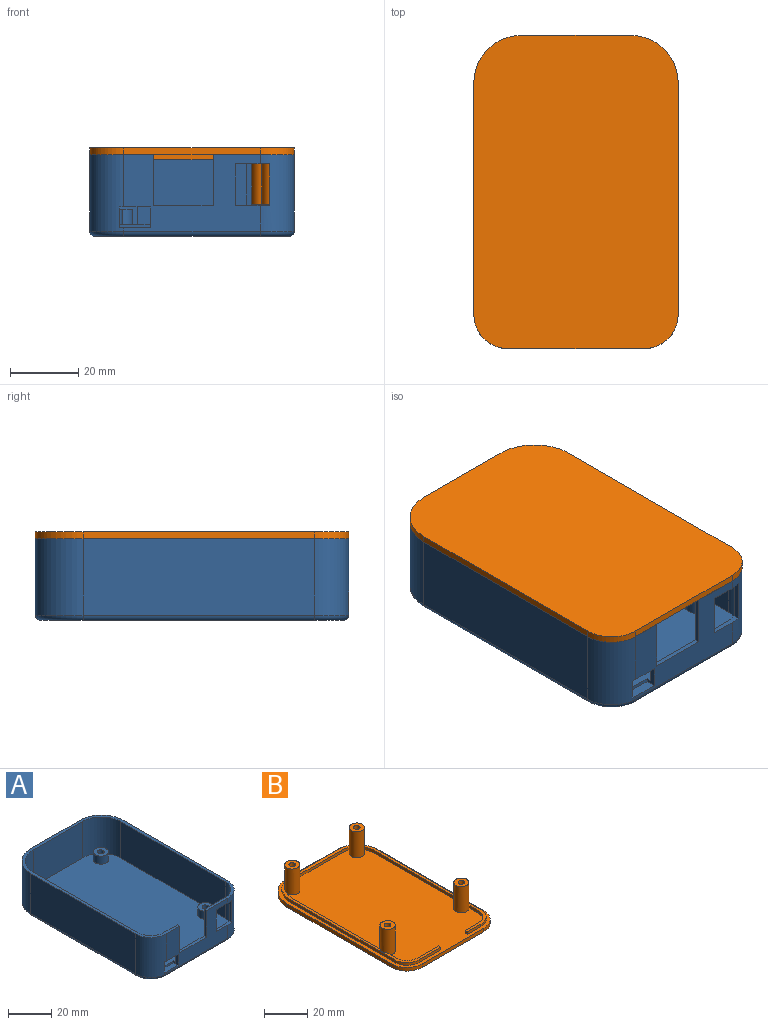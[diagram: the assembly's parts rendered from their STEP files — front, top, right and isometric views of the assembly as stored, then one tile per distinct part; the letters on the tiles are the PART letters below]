
ASSEMBLY  parts=2 mates=1
PART A: 59 faces, bbox 62.3x94x24 mm
  f0: plane 40x22.5mm, normal (0,-1,0), area 500.7mm2, adj f1,f2,f3,f39,f40,f42,f44,f45
  f1: plane 92x60mm, normal (0,0,1), area 391.8mm2, adj f0,f2,f3,f4,f5,f6,f11,f12
  f2: cylinder r=10mm len=22.5mm, axis (0,0,1), area 317.2mm2, adj f0,f1,f11,f45,f46,f47,f55
  f3: cylinder r=10mm len=22.5mm, axis (0,0,-1), area 345.5mm2, adj f0,f1,f13,f40,f41,f42,f51
  f4: plane 40x20.5mm, normal (0,1,0), area 428.4mm2, adj f1,f5,f6,f20,f39,f40,f44,f45
  f5: cylinder r=8.5mm len=20.5mm, axis (0,0,1), area 237.3mm2, adj f1,f4,f17,f20,f45,f46,f47
  f6: cylinder r=8.5mm len=20.5mm, axis (0,0,-1), area 267.1mm2, adj f1,f4,f19,f20,f40,f41
  f7: cylinder r=1.5mm len=6mm, axis (0,0,1), area 56.5mm2, adj f24,f37
  f8: cylinder r=1.5mm len=6mm, axis (0,0,1), area 56.5mm2, adj f30,f35
  f9: cylinder r=1.5mm len=6mm, axis (0,0,1), area 56.5mm2, adj f26,f33
  f10: cylinder r=1.5mm len=6mm, axis (0,0,1), area 56.5mm2, adj f28,f31
  f11: plane 68x22.5mm, normal (1,0,0), area 1530mm2, adj f1,f2,f15,f57
  f12: plane 32x22.5mm, normal (0,1,0), area 720mm2, adj f1,f15,f16,f56
  f13: plane 68x22.5mm, normal (-1,0,0), area 1530mm2, adj f1,f3,f16,f52
  f14: plane 89x57mm, normal (0,0,-1), area 4896.4mm2, adj f32,f34,f36,f38,f51,f52,f53,f54
  f15: cylinder r=14mm len=22.5mm, axis (0,0,-1), area 494.8mm2, adj f1,f11,f12,f58
  f16: cylinder r=14mm len=22.5mm, axis (0,0,1), area 494.8mm2, adj f1,f12,f13,f54
  f17: plane 68x20.5mm, normal (-1,0,0), area 1394mm2, adj f1,f5,f20,f21
  f18: plane 32x20.5mm, normal (0,-1,0), area 656mm2, adj f1,f20,f21,f22
  f19: plane 68x20.5mm, normal (1,0,0), area 1394mm2, adj f1,f6,f20,f22
  f20: plane 89x57mm, normal (0,0,1), area 4807.5mm2, adj f4,f5,f6,f17,f18,f19,f21,f22
  f21: cylinder r=12.5mm len=20.5mm, axis (0,0,-1), area 402.5mm2, adj f1,f17,f18,f20
  f22: cylinder r=12.5mm len=20.5mm, axis (0,0,1), area 402.5mm2, adj f1,f18,f19,f20
  f23: cylinder r=3.5mm len=7mm, axis (0,0,-1), area 99mm2, adj f20,f24
  f24: plane 7x7mm, normal (0,0,1), area 31.4mm2, adj f7,f23
  f25: cylinder r=3.5mm len=7mm, axis (0,0,-1), area 99mm2, adj f20,f26
  f26: plane 7x7mm, normal (0,0,1), area 31.4mm2, adj f9,f25
  f27: cylinder r=3.5mm len=7mm, axis (0,0,-1), area 99mm2, adj f20,f28
  f28: plane 7x7mm, normal (0,0,1), area 31.4mm2, adj f10,f27
  f29: cylinder r=3.5mm len=7mm, axis (0,0,-1), area 99mm2, adj f20,f30
  f30: plane 7x7mm, normal (0,0,1), area 31.4mm2, adj f8,f29
  f31: plane 5x5mm, normal (0,0,-1), area 12.6mm2, adj f10,f32
  f32: cylinder r=2.5mm len=5mm, axis (0,0,-1), area 31.4mm2, adj f14,f31
  f33: plane 5x5mm, normal (0,0,-1), area 12.6mm2, adj f9,f34
  f34: cylinder r=2.5mm len=5mm, axis (0,0,-1), area 31.4mm2, adj f14,f33
  f35: plane 5x5mm, normal (0,0,-1), area 12.6mm2, adj f8,f36
  f36: cylinder r=2.5mm len=5mm, axis (0,0,-1), area 31.4mm2, adj f14,f35
  f37: plane 5x5mm, normal (0,0,-1), area 12.6mm2, adj f7,f38
  f38: cylinder r=2.5mm len=5mm, axis (0,0,-1), area 31.4mm2, adj f14,f37
  f39: plane 6.1x3mm, normal (-1,0,0), area 10.7mm2, adj f0,f4,f20,f40,f42,f43
  f40: plane 9x1.6mm, normal (0,0,-1), area 13.5mm2, adj f0,f3,f4,f6,f39,f41
  f41: plane 6.1x2.92mm, normal (1,0,0), area 10.6mm2, adj f3,f6,f20,f40,f42,f43
  f42: plane 9x3mm, normal (0,0,1), area 27mm2, adj f0,f3,f39,f41,f43
  f43: plane 9x1mm, normal (0,-1,0), area 9mm2, adj f20,f39,f41,f42
  f44: plane 12.3x1.5mm, normal (1,0,0), area 18.5mm2, adj f0,f4,f45,f46
  f45: plane 10.2x2.01mm, normal (0,0,-1), area 15.4mm2, adj f0,f2,f4,f5,f44,f47
  f46: plane 10.2x2.01mm, normal (0,0,1), area 15.4mm2, adj f0,f2,f4,f5,f44,f47
  f47: plane 12.3x1.58mm, normal (-1,0,0), area 19.4mm2, adj f2,f5,f45,f46
  f48: plane 15x1.5mm, normal (1,0,0), area 22.5mm2, adj f0,f1,f4,f49
  f49: plane 17.5x1.5mm, normal (0,0,1), area 26.3mm2, adj f0,f4,f48,f50
  f50: plane 15x1.5mm, normal (-1,0,0), area 22.5mm2, adj f0,f1,f4,f49
  f51: torus R=8.5mm, axis (0,0,1), area 35mm2, adj f3,f14,f52,f53
  f52: cylinder r=1.5mm len=68mm, axis (0,-1,0), area 160.2mm2, adj f13,f14,f51,f54
  f53: cylinder r=1.5mm len=40mm, axis (1,0,0), area 94.2mm2, adj f0,f14,f51,f55
  f54: torus R=12.5mm, axis (0,0,1), area 49.8mm2, adj f14,f16,f52,f56
  f55: torus R=8.5mm, axis (0,0,1), area 35mm2, adj f2,f14,f53,f57
  f56: cylinder r=1.5mm len=32mm, axis (-1,0,0), area 75.4mm2, adj f12,f14,f54,f58
  f57: cylinder r=1.5mm len=68mm, axis (0,1,0), area 160.2mm2, adj f11,f14,f55,f58
  f58: torus R=12.5mm, axis (0,0,1), area 49.8mm2, adj f14,f15,f56,f57
PART B: 51 faces, bbox 60x92x16.6 mm
  f0: plane 92x60mm, normal (0,0,1), area 4870mm2, adj f1,f2,f3,f4,f5,f6,f7,f8
  f1: plane 57.27x1.5mm, normal (-1,0,0), area 85.9mm2, adj f0,f2,f34,f47
  f2: cylinder r=10.7mm len=6.83mm, axis (0,0,-1), area 11.1mm2, adj f0,f1,f34,f43
  f3: plane 6.27x1.5mm, normal (1,0,0), area 9.4mm2, adj f0,f16,f34,f40
  f4: plane 57.27x1.5mm, normal (1,0,0), area 85.9mm2, adj f0,f6,f34,f40
  f5: cylinder r=10.7mm len=6.01mm, axis (0,0,-1), area 9.6mm2, adj f0,f17,f34,f36
  f6: cylinder r=10.7mm len=6.83mm, axis (0,0,-1), area 11.1mm2, adj f0,f4,f34,f36
  f7: plane 40x2mm, normal (0,-1,0), area 80mm2, adj f0,f11,f12,f13
  f8: plane 68x2mm, normal (1,0,0), area 136mm2, adj f0,f11,f12,f14
  f9: plane 32x2mm, normal (0,1,0), area 64mm2, adj f0,f11,f14,f15
  f10: plane 68x2mm, normal (-1,0,0), area 136mm2, adj f0,f11,f13,f15
  f11: plane 92x60mm, normal (0,0,-1), area 5393mm2, adj f7,f8,f9,f10,f12,f13,f14,f15
  f12: cylinder r=10mm len=10mm, axis (0,0,1), area 31.4mm2, adj f0,f7,f8,f11
  f13: cylinder r=10mm len=10mm, axis (0,0,-1), area 31.4mm2, adj f0,f7,f10,f11
  f14: cylinder r=14mm len=14mm, axis (0,0,-1), area 44mm2, adj f0,f8,f9,f11
  f15: cylinder r=14mm len=14mm, axis (0,0,1), area 44mm2, adj f0,f9,f10,f11
  f16: cylinder r=6.7mm len=6.7mm, axis (0,0,-1), area 15.8mm2, adj f0,f3,f33,f34
  f17: plane 32x1.5mm, normal (0,-1,0), area 48mm2, adj f0,f5,f18,f34
  f18: cylinder r=10.7mm len=6.01mm, axis (0,0,-1), area 9.6mm2, adj f0,f17,f34,f43
  f19: plane 6.27x1.5mm, normal (-1,0,0), area 9.4mm2, adj f0,f20,f34,f47
  f20: cylinder r=6.7mm len=6.7mm, axis (0,0,-1), area 15.8mm2, adj f0,f19,f21,f34
  f21: plane 8.7x1.5mm, normal (0,1,0), area 13.1mm2, adj f0,f20,f22,f34
  f22: plane 1.5x1.5mm, normal (-1,0,0), area 2.3mm2, adj f0,f21,f23,f34
  f23: plane 8.7x1.5mm, normal (0,-1,0), area 13.1mm2, adj f0,f22,f24,f34
  f24: cylinder r=8.2mm len=8.2mm, axis (0,0,-1), area 19.3mm2, adj f0,f23,f25,f34
  f25: plane 68x1.5mm, normal (1,0,0), area 102mm2, adj f0,f24,f26,f34
  f26: cylinder r=12.2mm len=12.2mm, axis (0,0,-1), area 28.7mm2, adj f0,f25,f27,f34
  f27: plane 32x1.5mm, normal (0,1,0), area 48mm2, adj f0,f26,f28,f34
  f28: cylinder r=12.2mm len=12.2mm, axis (0,0,-1), area 28.7mm2, adj f0,f27,f29,f34
  f29: plane 68x1.5mm, normal (-1,0,0), area 102mm2, adj f0,f28,f30,f34
  f30: cylinder r=8.2mm len=8.2mm, axis (0,0,-1), area 19.3mm2, adj f0,f29,f31,f34
  f31: plane 13.8x1.5mm, normal (0,-1,0), area 20.7mm2, adj f0,f30,f32,f34
  f32: plane 1.5x1.5mm, normal (1,0,0), area 2.3mm2, adj f0,f31,f33,f34
  f33: plane 13.8x1.5mm, normal (0,1,0), area 20.7mm2, adj f0,f16,f32,f34
  f34: plane 88.4x56.4mm, normal (0,0,1), area 369mm2, adj f1,f2,f3,f4,f5,f6,f16,f17
  f35: cylinder r=1.5mm len=14.6mm, axis (0,0,-1), area 137.6mm2, adj f37,f38
  f36: cylinder r=3.5mm len=14.6mm, axis (0,0,-1), area 316.4mm2, adj f0,f5,f6,f34,f37
  f37: plane 7x7mm, normal (0,0,1), area 31.4mm2, adj f35,f36
  f38: plane 3x3mm, normal (0,0,1), area 7.1mm2, adj f35
  f39: cylinder r=1.5mm len=14.6mm, axis (0,0,-1), area 137.6mm2, adj f41,f42
  f40: cylinder r=3.5mm len=14.6mm, axis (0,0,-1), area 313.8mm2, adj f0,f3,f4,f34,f41
  f41: plane 7x7mm, normal (0,0,1), area 31.4mm2, adj f39,f40
  f42: plane 3x3mm, normal (0,0,1), area 7.1mm2, adj f39
  f43: cylinder r=3.5mm len=14.6mm, axis (0,0,-1), area 316.4mm2, adj f0,f2,f18,f34,f45
  f44: cylinder r=1.5mm len=14.6mm, axis (0,0,-1), area 137.6mm2, adj f45,f46
  f45: plane 7x7mm, normal (0,0,1), area 31.4mm2, adj f43,f44
  f46: plane 3x3mm, normal (0,0,1), area 7.1mm2, adj f44
  f47: cylinder r=3.5mm len=14.6mm, axis (0,0,-1), area 313.8mm2, adj f0,f1,f19,f34,f49
  f48: cylinder r=1.5mm len=14.6mm, axis (0,0,-1), area 137.6mm2, adj f49,f50
  f49: plane 7x7mm, normal (0,0,1), area 31.4mm2, adj f47,f48
  f50: plane 3x3mm, normal (0,0,1), area 7.1mm2, adj f48
PLACE A t=(-12.82,-34.49,-22.3)mm
PLACE B rot(axis=(0,1,0),180deg) t=(-12.82,-34.49,3.7)mm
MATE fastened B.f47 <-> A.f9  axis (0,0,-1) through (-36.82,-61.99,-12.9)mm
